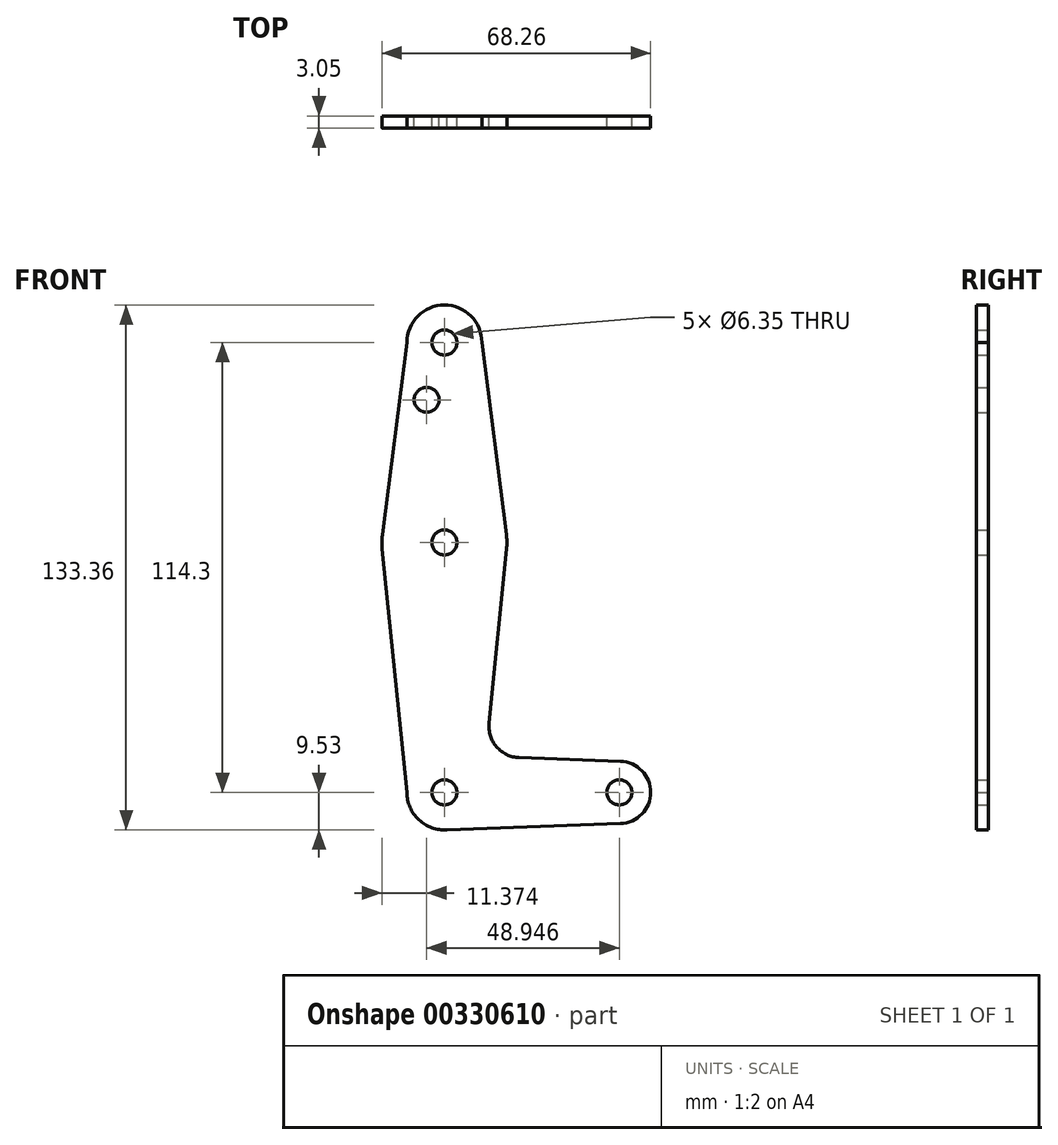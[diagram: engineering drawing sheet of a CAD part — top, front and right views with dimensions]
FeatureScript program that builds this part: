
annotation { "Feature Type Name" : "Feature", "Feature Type Description" : "" }
export const myFeature = defineFeature(function(context is Context, id is Id, definition is map)
    precondition{}
    {
        {
            var Q0;
            Q0=qCreatedBy(makeId("Front.planeOp"),FACE);
            var sketch = newSketch(context, id + "F0", { "sketchPlane" : qUnion([Q0])});
            skLineSegment(sketch, "E0", {"start": v(0, 0) * mm, "end": v(0, 114.3) * mm, "construction": true});
            skLineSegment(sketch, "E1", {"start": v(0, 114.3) * mm, "end": v(0, 104.77) * mm});
            skLineSegment(sketch, "E2", {"start": v(0, 0) * mm, "end": v(44.45, 0) * mm, "construction": true});
            skCircle(sketch, "E3", {"center": v(0, 114.3) * mm, "radius": 9.53 * mm});
            skCircle(sketch, "E4", {"center": v(0, 63.5) * mm, "radius": 15.88 * mm});
            skCircle(sketch, "E5", {"center": v(0, 0) * mm, "radius": 9.53 * mm});
            skCircle(sketch, "E6", {"center": v(44.45, 0) * mm, "radius": 7.94 * mm});
            skLineSegment(sketch, "E7", {"start": v(-9.53, 114.3) * mm, "end": v(-15.75, 65.5) * mm});
            skLineSegment(sketch, "E8", {"start": v(9.52, 114.3) * mm, "end": v(15.75, 65.5) * mm});
            skLineSegment(sketch, "E9.trimOffspring", {"start": v(0, 9.53) * mm, "end": v(0, 0) * mm});
            skCircle(sketch, "E10", {"center": v(0, 114.3) * mm, "radius": 3.18 * mm});
            skLineSegment(sketch, "E11", {"start": v(18.97, 8.85) * mm, "end": v(44.73, 7.93) * mm});
            skLineSegment(sketch, "E12", {"start": v(0, -9.53) * mm, "end": v(44.73, -7.93) * mm});
            skLineSegment(sketch, "E13", {"start": v(-9.52, 0) * mm, "end": v(-15.8, 61.9) * mm});
            skLineSegment(sketch, "E14", {"start": v(15.8, 61.9) * mm, "end": v(11.34, 17.59) * mm});
            skCircle(sketch, "E15", {"center": v(0, 63.5) * mm, "radius": 3.18 * mm});
            skCircle(sketch, "E16", {"center": v(0, 0) * mm, "radius": 3.18 * mm});
            skCircle(sketch, "E17", {"center": v(44.45, 0) * mm, "radius": 3.18 * mm});
            skCircle(sketch, "E18", {"center": v(-4.5, 99.75) * mm, "radius": 3.18 * mm});
            skPoint(sketch, "E19.newPointB", {"position": v(9.57, 0) * mm});
            skArc(sketch, "E19.filletArc", {"start": v(11.34, 17.59) * mm, "mid": v(13.26, 11.57) * mm, "end": v(18.97, 8.85) * mm});
            skSolve(sketch);
        }
        {
            var Q0;
            Q0 = qSketchRegion(id + "F0", true);
            extrude(context, id + "F1", {"entities" : qUnion([Q0]), "depth" : 3.05 * mm});
        }
    });
